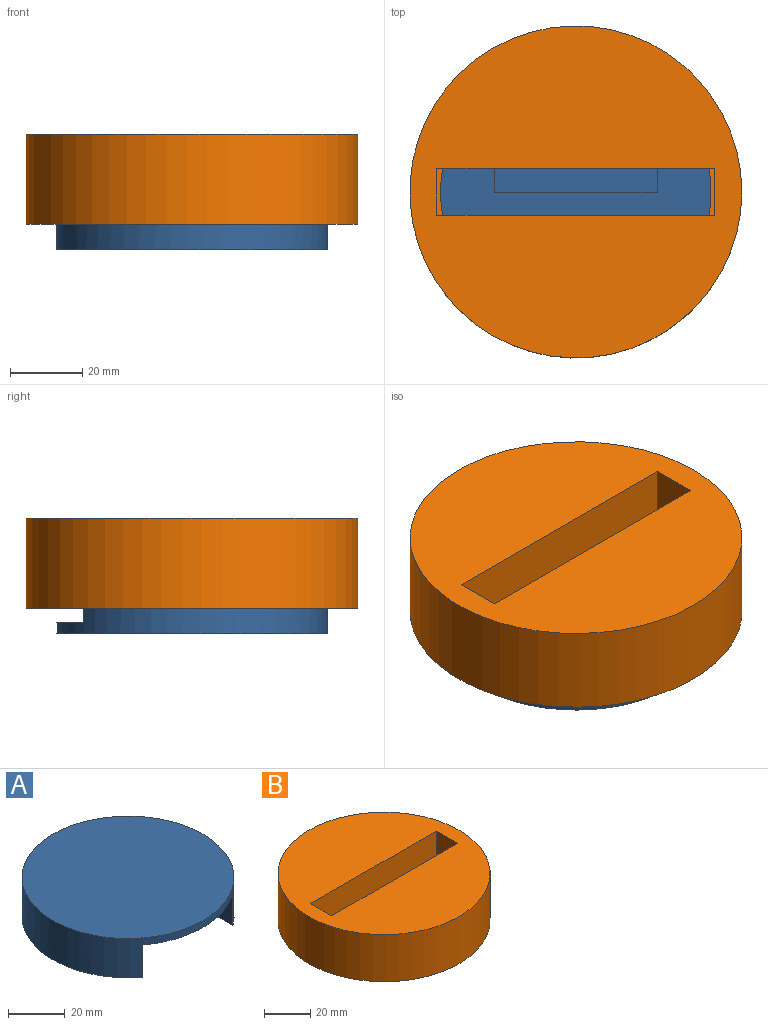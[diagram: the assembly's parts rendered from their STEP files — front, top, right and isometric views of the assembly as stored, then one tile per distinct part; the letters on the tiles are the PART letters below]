
ASSEMBLY  parts=2 mates=1
PART A: 7 faces, bbox 75x75x17 mm
  f0: plane 75x67.5mm, normal (0,0,-1), area 2837.9mm2, adj f1,f4,f5,f6
  f1: cylinder r=37.5mm len=75mm, axis (0,0,-1), area 3329.9mm2, adj f0,f2,f3,f4,f5
  f2: plane 75x75mm, normal (0,0,1), area 4417.9mm2, adj f1
  f3: plane 45x37.5mm, normal (0,0,-1), area 1579.9mm2, adj f1,f4,f5,f6
  f4: plane 30x14mm, normal (1,0,0), area 420mm2, adj f0,f1,f3,f6
  f5: plane 30x14mm, normal (-1,0,0), area 420mm2, adj f0,f1,f3,f6
  f6: plane 45x14mm, normal (0,-1,0), area 630mm2, adj f0,f3,f4,f5
PART B: 15 faces, bbox 92x92x25 mm
  f0: plane 73.86x35mm, normal (0,0,-1), area 1972.1mm2, adj f4,f5,f6,f7,f12
  f1: cylinder r=46mm len=92mm, axis (0,0,-1), area 7225.7mm2, adj f2,f3
  f2: plane 92x92mm, normal (0,0,1), area 5646.6mm2, adj f1,f11,f12,f13,f14
  f3: plane 92x92mm, normal (0,0,-1), area 1981.6mm2, adj f1,f4,f5,f6,f7
  f4: plane 10x2.83mm, normal (0.71,0.71,0), area 40mm2, adj f0,f3,f5,f7
  f5: cylinder r=41.5mm len=58.69mm, axis (0,0,-1), area 651.9mm2, adj f0,f3,f4,f6
  f6: plane 10x2.83mm, normal (-0.71,0.71,0), area 40mm2, adj f0,f3,f5,f7
  f7: cylinder r=37.5mm len=75mm, axis (0,0,-1), area 1767.1mm2, adj f0,f3,f4,f6,f8,f9,f10
  f8: plane 73.86x31mm, normal (0,0,-1), area 1723.9mm2, adj f7,f14
  f9: plane 13x1.57mm, normal (0,0,1), area 15.5mm2, adj f7,f11,f12,f14
  f10: plane 13x1.57mm, normal (0,0,1), area 15.5mm2, adj f7,f12,f13,f14
  f11: plane 15x13mm, normal (-1,0,0), area 195mm2, adj f2,f9,f12,f14
  f12: plane 77x15mm, normal (0,-1,0), area 1155mm2, adj f0,f2,f9,f10,f11,f13
  f13: plane 15x13mm, normal (1,0,0), area 195mm2, adj f2,f10,f12,f14
  f14: plane 77x15mm, normal (0,1,0), area 1155mm2, adj f2,f8,f9,f10,f11,f13
PLACE A rot(axis=(-1,0,0),180deg) t=(0,-0.08,-2.42)mm
PLACE B t=(0,-0.08,-12.42)mm
MATE planar B.f5 <-> A.f1  axis (0,0,-1) through (0,-0.08,-2.42)mm
